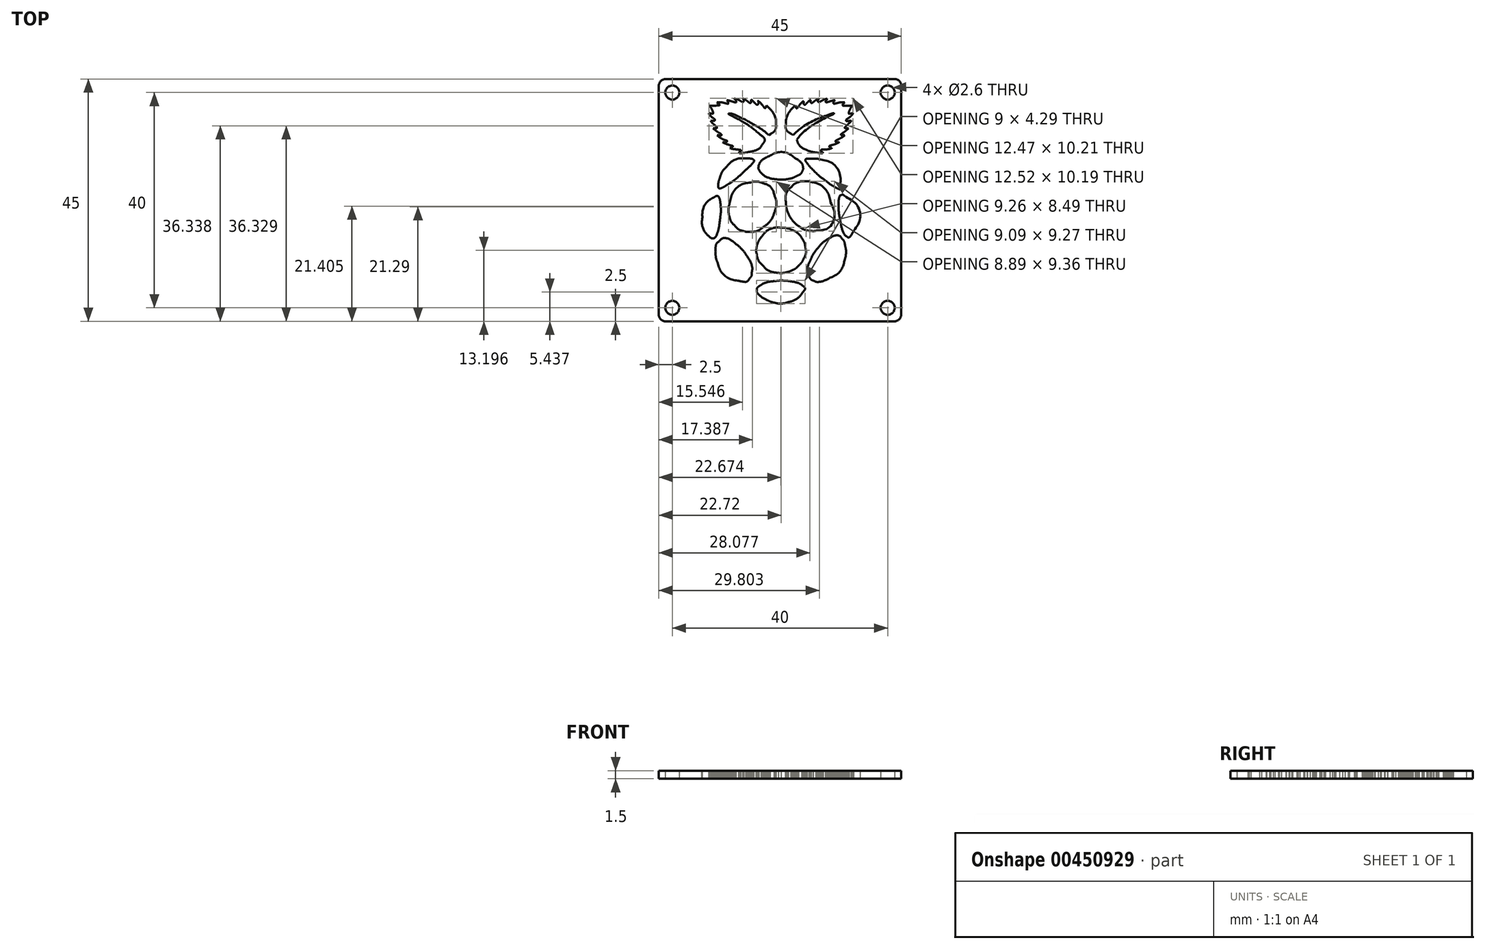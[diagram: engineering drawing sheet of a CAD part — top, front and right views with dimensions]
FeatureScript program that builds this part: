
annotation { "Feature Type Name" : "Feature", "Feature Type Description" : "" }
export const myFeature = defineFeature(function(context is Context, id is Id, definition is map)
    precondition{}
    {
        {
            var Q0;
            Q0=qCreatedBy(makeId("Top.planeOp"),FACE);
            var sketch = newSketch(context, id + "F0", { "sketchPlane" : qUnion([Q0])});
            skLineSegment(sketch, "E0.bottom", {"start": v(20, -20) * mm, "end": v(-20, -20) * mm});
            skLineSegment(sketch, "E0.top", {"start": v(20, 20) * mm, "end": v(-20, 20) * mm});
            skLineSegment(sketch, "E0.left", {"start": v(20, -20) * mm, "end": v(20, 20) * mm});
            skLineSegment(sketch, "E0.right", {"start": v(-20, -20) * mm, "end": v(-20, 20) * mm});
            skPoint(sketch, "E0.middle", {"position": v(0, 0) * mm});
            skSolve(sketch);
        }
        {
            var Q0;
            Q0=qCreatedBy(makeId("Top.planeOp"),FACE);
            var sketch = newSketch(context, id + "F1", { "sketchPlane" : qUnion([Q0])});
            skLineSegment(sketch, "E1.bottom", {"start": v(22.5, -22.5) * mm, "end": v(-22.5, -22.5) * mm});
            skLineSegment(sketch, "E1.top", {"start": v(22.5, 22.5) * mm, "end": v(-22.5, 22.5) * mm});
            skLineSegment(sketch, "E1.left", {"start": v(22.5, -22.5) * mm, "end": v(22.5, 22.5) * mm});
            skLineSegment(sketch, "E1.right", {"start": v(-22.5, -22.5) * mm, "end": v(-22.5, 22.5) * mm});
            skPoint(sketch, "E1.middle", {"position": v(0, 0) * mm});
            skSolve(sketch);
        }
        {
            var Q0;
            Q0=qCreatedBy(makeId("Top.planeOp"),FACE);
            var sketch = newSketch(context, id + "F2", { "sketchPlane" : qUnion([Q0])});
            skCircle(sketch, "E2", {"center": v(-20, 20) * mm, "radius": 1.3 * mm});
            skCircle(sketch, "E3", {"center": v(20, 20) * mm, "radius": 1.3 * mm});
            skCircle(sketch, "E4", {"center": v(-20, -20) * mm, "radius": 1.3 * mm});
            skCircle(sketch, "E5", {"center": v(20, -20) * mm, "radius": 1.3 * mm});
            skSolve(sketch);
        }
        {
            var Q0;
            Q0 = qSketchRegion(id + "F1", true);
            extrude(context, id + "F3", {"entities" : qUnion([Q0]), "depth" : 1.5 * mm, "offsetDistance" : 25 * mm});
        }
        {
            var Q0;
            Q0 = qSketchRegion(id + "F0", true);
            extrude(context, id + "F4", {"entities" : qUnion([Q0]), "operationType" : NewBodyOperationType.ADD, "depth" : 1.5 * mm, "offsetDistance" : 25 * mm});
        }
        {
            var Q0;
            Q0 = qSketchRegion(id + "F2", true);
            extrude(context, id + "F5", {"entities" : qUnion([Q0]), "operationType" : NewBodyOperationType.REMOVE, "flatOperationType" : FlatOperationType.REMOVE, "depth" : 1.5 * mm, "offsetDistance" : 25 * mm, "domain" : OperationDomain.MODEL});
        }
        {
            var Q0;
            Q0=makeQuery(id+"F3.opExtrude","SWEPT_EDGE",EDGE,{"disambiguationData":[OSD([sQuery(id+"F1.wireOp",EDGE,"E1.top"),sQuery(id+"F1.wireOp",EDGE,"E1.left")])]});
            var Q1;
            Q1=makeQuery(id+"F3.opExtrude","SWEPT_EDGE",EDGE,{"disambiguationData":[OSD([sQuery(id+"F1.wireOp",EDGE,"E1.top"),sQuery(id+"F1.wireOp",EDGE,"E1.right")])]});
            var Q2;
            Q2=makeQuery(id+"F3.opExtrude","SWEPT_EDGE",EDGE,{"disambiguationData":[OSD([sQuery(id+"F1.wireOp",EDGE,"E1.bottom"),sQuery(id+"F1.wireOp",EDGE,"E1.right")])]});
            var Q3;
            Q3=makeQuery(id+"F3.opExtrude","SWEPT_EDGE",EDGE,{"disambiguationData":[OSD([sQuery(id+"F1.wireOp",EDGE,"E1.bottom"),sQuery(id+"F1.wireOp",EDGE,"E1.left")])]});
            fillet(context, id + "F6", {"entities" : qUnion([Q0, Q1, Q2, Q3]), "radius" : 1.2 * mm, "tangentPropagation" : true, "allowEdgeOverflow" : false});
        }
        {
            var Q0;
            Q0=qCreatedBy(makeId("Top.planeOp"),FACE);
            cPlane(context, id + "F7", {"entities" : qUnion([Q0]), "cplaneType" : CPlaneType.OFFSET, "offset" : 25 * mm, "width" : 150 * mm, "height" : 150 * mm});
        }
        {
            var Q0;
            Q0=qCreatedBy(id+"F7.planeOp",FACE);
            var sketch = newSketch(context, id + "F8", { "sketchPlane" : qUnion([Q0])});
            skFitSpline(sketch, "E6", {"points": [v(-0.89, -19.07) * mm, v(-1.37, -18.96) * mm, v(-1.92, -18.78) * mm, v(-2.27, -18.6) * mm]});
            skFitSpline(sketch, "E7", {"points": [v(-2.27, -18.6) * mm, v(-3.23, -18.12) * mm, v(-4.29, -17.1) * mm, v(-4.29, -16.67) * mm]});
            skFitSpline(sketch, "E8", {"points": [v(-4.29, -16.67) * mm, v(-4.29, -16.4) * mm, v(-4, -16.06) * mm, v(-3.5, -15.74) * mm]});
            skFitSpline(sketch, "E9", {"points": [v(-3.5, -15.74) * mm, v(-2.99, -15.43) * mm, v(-1.93, -15.14) * mm, v(-0.78, -15) * mm]});
            skFitSpline(sketch, "E10", {"points": [v(-0.78, -15) * mm, v(-0.11, -14.93) * mm, v(1.32, -14.97) * mm, v(2.07, -15.1) * mm]});
            skFitSpline(sketch, "E11", {"points": [v(2.07, -15.1) * mm, v(2.83, -15.22) * mm, v(3.85, -15.59) * mm, v(4.15, -15.85) * mm]});
            skFitSpline(sketch, "E12", {"points": [v(4.15, -15.85) * mm, v(4.62, -16.25) * mm, v(4.65, -16.56) * mm, v(4.27, -17.04) * mm]});
            skFitSpline(sketch, "E13", {"points": [v(4.27, -17.04) * mm, v(3.53, -17.98) * mm, v(2.59, -18.62) * mm, v(1.46, -18.95) * mm]});
            skFitSpline(sketch, "E14", {"points": [v(1.46, -18.95) * mm, v(0.83, -19.14) * mm, v(-0.3, -19.2) * mm, v(-0.89, -19.07) * mm]});
            skFitSpline(sketch, "E15", {"points": [v(-7.64, -14.96) * mm, v(-9.38, -14.6) * mm, v(-10.94, -13.25) * mm, v(-11.6, -11.56) * mm]});
            skFitSpline(sketch, "E16", {"points": [v(-11.6, -11.56) * mm, v(-11.84, -10.92) * mm, v(-11.94, -10.32) * mm, v(-11.94, -9.57) * mm]});
            skFitSpline(sketch, "E17", {"points": [v(-11.94, -9.57) * mm, v(-11.94, -8.58) * mm, v(-11.75, -8) * mm, v(-11.3, -7.65) * mm]});
            skFitSpline(sketch, "E18", {"points": [v(-11.3, -7.65) * mm, v(-10.56, -7.05) * mm, v(-9.4, -7.25) * mm, v(-8.08, -8.22) * mm]});
            skFitSpline(sketch, "E19", {"points": [v(-8.08, -8.22) * mm, v(-7.62, -8.56) * mm, v(-6.63, -9.62) * mm, v(-6.3, -10.13) * mm]});
            skFitSpline(sketch, "E20", {"points": [v(-6.3, -10.13) * mm, v(-5.55, -11.3) * mm, v(-5.15, -12.47) * mm, v(-5.22, -13.34) * mm]});
            skFitSpline(sketch, "E21", {"points": [v(-5.22, -13.34) * mm, v(-5.26, -13.97) * mm, v(-5.32, -14.14) * mm, v(-5.61, -14.51) * mm]});
            skFitSpline(sketch, "E22", {"points": [v(-5.61, -14.51) * mm, v(-6.04, -15.06) * mm, v(-6.6, -15.18) * mm, v(-7.64, -14.96) * mm]});
            skFitSpline(sketch, "E23", {"points": [v(6.26, -14.97) * mm, v(5.9, -14.83) * mm, v(5.61, -14.57) * mm, v(5.42, -14.18) * mm]});
            skFitSpline(sketch, "E24", {"points": [v(5.42, -14.18) * mm, v(5.14, -13.6) * mm, v(5.2, -12.22) * mm, v(5.54, -11.43) * mm]});
            skFitSpline(sketch, "E25", {"points": [v(5.54, -11.43) * mm, v(5.58, -11.33) * mm, v(5.68, -11.09) * mm, v(5.76, -10.9) * mm]});
            skFitSpline(sketch, "E26", {"points": [v(5.76, -10.9) * mm, v(5.95, -10.44) * mm, v(6.61, -9.4) * mm, v(7.07, -8.84) * mm]});
            skFitSpline(sketch, "E27", {"points": [v(7.07, -8.84) * mm, v(7.54, -8.27) * mm, v(8.45, -7.48) * mm, v(9, -7.17) * mm]});
            skFitSpline(sketch, "E28", {"points": [v(9, -7.17) * mm, v(10.02, -6.6) * mm, v(11, -6.6) * mm, v(11.53, -7.15) * mm]});
            skFitSpline(sketch, "E29", {"points": [v(11.53, -7.15) * mm, v(11.81, -7.46) * mm, v(12, -7.92) * mm, v(12.15, -8.71) * mm]});
            skFitSpline(sketch, "E30", {"points": [v(12.15, -8.71) * mm, v(12.26, -9.3) * mm, v(12.19, -10.46) * mm, v(12, -11.07) * mm]});
            skFitSpline(sketch, "E31", {"points": [v(12, -11.07) * mm, v(11.55, -12.6) * mm, v(10.56, -13.78) * mm, v(9.13, -14.49) * mm]});
            skFitSpline(sketch, "E32", {"points": [v(9.13, -14.49) * mm, v(8.17, -14.97) * mm, v(6.87, -15.18) * mm, v(6.26, -14.97) * mm]});
            skFitSpline(sketch, "E33", {"points": [v(-0.24, -13.5) * mm, v(-1.52, -13.32) * mm, v(-2.45, -12.9) * mm, v(-3.16, -12.15) * mm]});
            skFitSpline(sketch, "E34", {"points": [v(-3.16, -12.15) * mm, v(-3.83, -11.45) * mm, v(-4.16, -10.82) * mm, v(-4.34, -9.89) * mm]});
            skFitSpline(sketch, "E35", {"points": [v(-4.34, -9.89) * mm, v(-4.4, -9.51) * mm, v(-4.32, -8.56) * mm, v(-4.17, -8.13) * mm]});
            skFitSpline(sketch, "E36", {"points": [v(-4.17, -8.13) * mm, v(-4.04, -7.74) * mm, v(-3.6, -6.98) * mm, v(-3.3, -6.65) * mm]});
            skFitSpline(sketch, "E37", {"points": [v(-3.3, -6.65) * mm, v(-2.5, -5.73) * mm, v(-1.04, -5.1) * mm, v(0.26, -5.1) * mm]});
            skFitSpline(sketch, "E38", {"points": [v(0.26, -5.1) * mm, v(0.76, -5.1) * mm, v(1.69, -5.3) * mm, v(2.2, -5.51) * mm]});
            skFitSpline(sketch, "E39", {"points": [v(2.2, -5.51) * mm, v(2.86, -5.79) * mm, v(3.66, -6.46) * mm, v(4.07, -7.1) * mm]});
            skFitSpline(sketch, "E40", {"points": [v(4.07, -7.1) * mm, v(4.44, -7.66) * mm, v(4.6, -8.02) * mm, v(4.7, -8.63) * mm]});
            skFitSpline(sketch, "E41", {"points": [v(4.7, -8.63) * mm, v(4.85, -9.48) * mm, v(4.74, -10.17) * mm, v(4.31, -11.04) * mm]});
            skFitSpline(sketch, "E42", {"points": [v(4.31, -11.04) * mm, v(4.11, -11.45) * mm, v(3.98, -11.62) * mm, v(3.5, -12.1) * mm]});
            skFitSpline(sketch, "E43", {"points": [v(3.5, -12.1) * mm, v(3, -12.6) * mm, v(2.87, -12.7) * mm, v(2.34, -12.96) * mm]});
            skFitSpline(sketch, "E44", {"points": [v(2.34, -12.96) * mm, v(2.02, -13.13) * mm, v(1.54, -13.3) * mm, v(1.3, -13.37) * mm]});
            skFitSpline(sketch, "E45", {"points": [v(1.3, -13.37) * mm, v(0.83, -13.48) * mm, v(0.06, -13.55) * mm, v(-0.24, -13.5) * mm]});
            skFitSpline(sketch, "E46", {"points": [v(-13.18, -6.7) * mm, v(-14, -5.84) * mm, v(-14.48, -4.45) * mm, v(-14.4, -3.23) * mm]});
            skFitSpline(sketch, "E47", {"points": [v(-14.4, -3.23) * mm, v(-14.32, -1.7) * mm, v(-13.48, -0.26) * mm, v(-12.2, 0.58) * mm]});
            skFitSpline(sketch, "E48", {"points": [v(-12.2, 0.58) * mm, v(-12.01, 0.7) * mm, v(-11.82, 0.8) * mm, v(-11.77, 0.8) * mm]});
            skFitSpline(sketch, "E49", {"points": [v(-11.77, 0.8) * mm, v(-11.5, 0.8) * mm, v(-11.2, 0.21) * mm, v(-11.09, -0.45) * mm]});
            skFitSpline(sketch, "E50", {"points": [v(-11.09, -0.45) * mm, v(-11.02, -0.92) * mm, v(-11, -2.43) * mm, v(-11.06, -2.86) * mm]});
            skFitSpline(sketch, "E51", {"points": [v(-11.06, -2.86) * mm, v(-11.38, -5.19) * mm, v(-12.15, -7.03) * mm, v(-12.8, -7.03) * mm]});
            skFitSpline(sketch, "E52", {"points": [v(-12.8, -7.03) * mm, v(-12.83, -7.03) * mm, v(-13, -6.88) * mm, v(-13.18, -6.7) * mm]});
            skFitSpline(sketch, "E53", {"points": [v(12.4, -6.74) * mm, v(11.97, -6.36) * mm, v(11.48, -5.18) * mm, v(11.23, -3.94) * mm]});
            skFitSpline(sketch, "E54", {"points": [v(11.23, -3.94) * mm, v(11.04, -3) * mm, v(10.9, -1.78) * mm, v(10.9, -1.14) * mm]});
            skFitSpline(sketch, "E55", {"points": [v(10.9, -1.14) * mm, v(10.9, -0.09) * mm, v(11.13, 0.83) * mm, v(11.42, 0.97) * mm]});
            skFitSpline(sketch, "E56", {"points": [v(11.42, 0.97) * mm, v(11.59, 1.04) * mm, v(11.84, 0.93) * mm, v(12.3, 0.6) * mm]});
            skFitSpline(sketch, "E57", {"points": [v(12.3, 0.6) * mm, v(14.3, -0.91) * mm, v(14.88, -3.45) * mm, v(13.72, -5.6) * mm]});
            skFitSpline(sketch, "E58", {"points": [v(13.72, -5.6) * mm, v(13.4, -6.22) * mm, v(12.82, -6.91) * mm, v(12.64, -6.91) * mm]});
            skFitSpline(sketch, "E59", {"points": [v(12.64, -6.91) * mm, v(12.62, -6.91) * mm, v(12.51, -6.83) * mm, v(12.4, -6.74) * mm]});
            skFitSpline(sketch, "E60", {"points": [v(-6.67, -5.76) * mm, v(-7.4, -5.56) * mm, v(-7.81, -5.32) * mm, v(-8.37, -4.76) * mm]});
            skFitSpline(sketch, "E61", {"points": [v(-8.37, -4.76) * mm, v(-8.9, -4.23) * mm, v(-9.18, -3.75) * mm, v(-9.37, -3.06) * mm]});
            skFitSpline(sketch, "E62", {"points": [v(-9.37, -3.06) * mm, v(-9.52, -2.5) * mm, v(-9.5, -1.2) * mm, v(-9.34, -0.62) * mm]});
            skFitSpline(sketch, "E63", {"points": [v(-9.34, -0.62) * mm, v(-8.79, 1.32) * mm, v(-7.3, 2.83) * mm, v(-5.48, 3.3) * mm]});
            skFitSpline(sketch, "E64", {"points": [v(-5.48, 3.3) * mm, v(-4.87, 3.45) * mm, v(-3.93, 3.42) * mm, v(-3.42, 3.24) * mm]});
            skFitSpline(sketch, "E65", {"points": [v(-3.42, 3.24) * mm, v(-2.14, 2.78) * mm, v(-1.41, 2.02) * mm, v(-0.97, 0.7) * mm]});
            skFitSpline(sketch, "E66", {"points": [v(-0.97, 0.7) * mm, v(-0.7, -0.09) * mm, v(-0.74, -1.3) * mm, v(-1.05, -2.21) * mm]});
            skFitSpline(sketch, "E67", {"points": [v(-1.05, -2.21) * mm, v(-1.4, -3.23) * mm, v(-2.17, -4.28) * mm, v(-3.04, -4.93) * mm]});
            skFitSpline(sketch, "E68", {"points": [v(-3.04, -4.93) * mm, v(-3.86, -5.54) * mm, v(-4.65, -5.83) * mm, v(-5.59, -5.87) * mm]});
            skFitSpline(sketch, "E69", {"points": [v(-5.59, -5.87) * mm, v(-6.09, -5.9) * mm, v(-6.26, -5.87) * mm, v(-6.67, -5.76) * mm]});
            skFitSpline(sketch, "E70", {"points": [v(5.69, -5.68) * mm, v(5, -5.61) * mm, v(4.16, -5.28) * mm, v(3.48, -4.81) * mm]});
            skFitSpline(sketch, "E71", {"points": [v(3.48, -4.81) * mm, v(3.16, -4.6) * mm, v(2.43, -3.88) * mm, v(2.16, -3.51) * mm]});
            skFitSpline(sketch, "E72", {"points": [v(2.16, -3.51) * mm, v(1.91, -3.18) * mm, v(1.37, -2.04) * mm, v(1.26, -1.61) * mm]});
            skFitSpline(sketch, "E73", {"points": [v(1.26, -1.61) * mm, v(1.2, -1.4) * mm, v(1.13, -0.92) * mm, v(1.12, -0.57) * mm]});
            skFitSpline(sketch, "E74", {"points": [v(1.12, -0.57) * mm, v(1.05, 0.72) * mm, v(1.4, 1.72) * mm, v(2.22, 2.57) * mm]});
            skFitSpline(sketch, "E75", {"points": [v(2.22, 2.57) * mm, v(2.58, 2.93) * mm, v(2.92, 3.15) * mm, v(3.5, 3.38) * mm]});
            skFitSpline(sketch, "E76", {"points": [v(3.5, 3.38) * mm, v(3.86, 3.52) * mm, v(3.98, 3.54) * mm, v(4.6, 3.54) * mm]});
            skFitSpline(sketch, "E77", {"points": [v(4.6, 3.54) * mm, v(5.2, 3.54) * mm, v(5.39, 3.52) * mm, v(5.74, 3.4) * mm]});
            skFitSpline(sketch, "E78", {"points": [v(5.74, 3.4) * mm, v(7.47, 2.87) * mm, v(8.85, 1.45) * mm, v(9.39, -0.34) * mm]});
            skFitSpline(sketch, "E79", {"points": [v(9.39, -0.34) * mm, v(10.14, -2.83) * mm, v(9, -5.13) * mm, v(6.78, -5.63) * mm]});
            skFitSpline(sketch, "E80", {"points": [v(6.78, -5.63) * mm, v(6.4, -5.72) * mm, v(6.14, -5.73) * mm, v(5.69, -5.68) * mm]});
            skFitSpline(sketch, "E81", {"points": [v(10.42, 2.35) * mm, v(9.77, 2.7) * mm, v(9.34, 2.96) * mm, v(8.91, 3.29) * mm]});
            skFitSpline(sketch, "E82", {"points": [v(8.91, 3.29) * mm, v(8.71, 3.44) * mm, v(8.32, 3.75) * mm, v(8.04, 3.96) * mm]});
            skFitSpline(sketch, "E83", {"points": [v(8.04, 3.96) * mm, v(7.28, 4.53) * mm, v(5.7, 6.07) * mm, v(5.11, 6.8) * mm]});
            skFitSpline(sketch, "E84", {"points": [v(5.11, 6.8) * mm, v(4.86, 7.11) * mm, v(4.7, 7.4) * mm, v(4.74, 7.5) * mm]});
            skFitSpline(sketch, "E85", {"points": [v(4.74, 7.5) * mm, v(4.8, 7.65) * mm, v(5.35, 7.73) * mm, v(6.17, 7.73) * mm]});
            skFitSpline(sketch, "E86", {"points": [v(6.17, 7.73) * mm, v(6.85, 7.72) * mm, v(7.03, 7.7) * mm, v(7.46, 7.57) * mm]});
            skFitSpline(sketch, "E87", {"points": [v(7.46, 7.57) * mm, v(9.63, 6.92) * mm, v(11.05, 5.14) * mm, v(11.22, 2.88) * mm]});
            skFitSpline(sketch, "E88", {"points": [v(11.22, 2.88) * mm, v(11.24, 2.61) * mm, v(11.24, 2.33) * mm, v(11.22, 2.25) * mm]});
            skFitSpline(sketch, "E89", {"points": [v(11.22, 2.25) * mm, v(11.16, 2.03) * mm, v(10.96, 2.06) * mm, v(10.42, 2.35) * mm]});
            skFitSpline(sketch, "E90", {"points": [v(-11.4, 2.3) * mm, v(-11.5, 2.57) * mm, v(-11.35, 3.6) * mm, v(-11.12, 4.28) * mm]});
            skFitSpline(sketch, "E91", {"points": [v(-11.12, 4.28) * mm, v(-10.85, 5.07) * mm, v(-10.48, 5.66) * mm, v(-9.84, 6.3) * mm]});
            skFitSpline(sketch, "E92", {"points": [v(-9.84, 6.3) * mm, v(-8.89, 7.24) * mm, v(-7.6, 7.77) * mm, v(-6.25, 7.76) * mm]});
            skFitSpline(sketch, "E93", {"points": [v(-6.25, 7.76) * mm, v(-5.72, 7.76) * mm, v(-5.06, 7.65) * mm, v(-4.96, 7.55) * mm]});
            skFitSpline(sketch, "E94", {"points": [v(-4.96, 7.55) * mm, v(-4.78, 7.37) * mm, v(-5.52, 6.4) * mm, v(-6.64, 5.36) * mm]});
            skFitSpline(sketch, "E95", {"points": [v(-6.64, 5.36) * mm, v(-7.54, 4.53) * mm, v(-8.96, 3.38) * mm, v(-9.5, 3.06) * mm]});
            skFitSpline(sketch, "E96", {"points": [v(-9.5, 3.06) * mm, v(-9.67, 2.95) * mm, v(-9.95, 2.78) * mm, v(-10.11, 2.67) * mm]});
            skFitSpline(sketch, "E97", {"points": [v(-10.11, 2.67) * mm, v(-10.46, 2.46) * mm, v(-11.05, 2.21) * mm, v(-11.23, 2.21) * mm]});
            skFitSpline(sketch, "E98", {"points": [v(-11.23, 2.21) * mm, v(-11.3, 2.21) * mm, v(-11.37, 2.25) * mm, v(-11.4, 2.3) * mm]});
            skFitSpline(sketch, "E99", {"points": [v(-0.76, 3.91) * mm, v(-1.66, 4.03) * mm, v(-2.9, 4.54) * mm, v(-3.41, 5) * mm]});
            skFitSpline(sketch, "E100", {"points": [v(-3.41, 5) * mm, v(-3.57, 5.14) * mm, v(-3.76, 5.4) * mm, v(-3.85, 5.58) * mm]});
            skFitSpline(sketch, "E101", {"points": [v(-3.85, 5.58) * mm, v(-4, 5.86) * mm, v(-4.01, 5.95) * mm, v(-3.99, 6.2) * mm]});
            skFitSpline(sketch, "E102", {"points": [v(-3.99, 6.2) * mm, v(-3.97, 6.37) * mm, v(-3.91, 6.59) * mm, v(-3.86, 6.7) * mm]});
            skFitSpline(sketch, "E103", {"points": [v(-3.86, 6.7) * mm, v(-3.62, 7.15) * mm, v(-2.73, 7.86) * mm, v(-1.94, 8.21) * mm]});
            skFitSpline(sketch, "E104", {"points": [v(-1.94, 8.21) * mm, v(-0.43, 8.9) * mm, v(1.35, 8.75) * mm, v(2.77, 7.85) * mm]});
            skFitSpline(sketch, "E105", {"points": [v(2.77, 7.85) * mm, v(3.6, 7.32) * mm, v(4.16, 6.68) * mm, v(4.27, 6.15) * mm]});
            skFitSpline(sketch, "E106", {"points": [v(4.27, 6.15) * mm, v(4.33, 5.88) * mm, v(4.32, 5.81) * mm, v(4.22, 5.58) * mm]});
            skFitSpline(sketch, "E107", {"points": [v(4.22, 5.58) * mm, v(3.98, 5.04) * mm, v(3.7, 4.78) * mm, v(2.94, 4.42) * mm]});
            skFitSpline(sketch, "E108", {"points": [v(2.94, 4.42) * mm, v(2.37, 4.15) * mm, v(2.15, 4.07) * mm, v(1.6, 3.97) * mm]});
            skFitSpline(sketch, "E109", {"points": [v(1.6, 3.97) * mm, v(0.92, 3.85) * mm, v(-0.06, 3.82) * mm, v(-0.76, 3.91) * mm]});
            skFitSpline(sketch, "E110", {"points": [v(-7.58, 8.81) * mm, v(-7.6, 8.83) * mm, v(-7.55, 8.91) * mm, v(-7.46, 9) * mm]});
            skFitSpline(sketch, "E111", {"points": [v(-7.46, 9) * mm, v(-7.36, 9.07) * mm, v(-7.29, 9.18) * mm, v(-7.29, 9.24) * mm]});
            skFitSpline(sketch, "E112", {"points": [v(-7.29, 9.24) * mm, v(-7.29, 9.36) * mm, v(-7.31, 9.36) * mm, v(-8.22, 9.46) * mm]});
            skFitSpline(sketch, "E113", {"points": [v(-8.22, 9.46) * mm, v(-8.54, 9.49) * mm, v(-8.9, 9.55) * mm, v(-9.05, 9.6) * mm]});
            skFitSpline(sketch, "E114", {"points": [v(-9.07, 9.78) * mm, v(-8.8, 9.9) * mm, v(-8.77, 10.08) * mm, v(-8.99, 10.15) * mm]});
            skFitSpline(sketch, "E115", {"points": [v(-8.99, 10.15) * mm, v(-9.54, 10.3) * mm, v(-10.3, 10.57) * mm, v(-10.46, 10.66) * mm]});
            skLineSegment(sketch, "E116", {"start": v(-9.05, 9.6) * mm, "end": v(-9.3, 9.67) * mm});
            skLineSegment(sketch, "E117", {"start": v(-9.3, 9.67) * mm, "end": v(-9.07, 9.78) * mm});
            skLineSegment(sketch, "E118", {"start": v(-9.07, 9.78) * mm, "end": v(-9.05, 9.6) * mm});
            skFitSpline(sketch, "E119", {"points": [v(-10.48, 10.76) * mm, v(-10, 10.77) * mm, v(-9.84, 11.02) * mm, v(-10.24, 11.18) * mm]});
            skFitSpline(sketch, "E120", {"points": [v(-10.24, 11.18) * mm, v(-10.53, 11.3) * mm, v(-11.28, 11.73) * mm, v(-11.51, 11.92) * mm]});
            skLineSegment(sketch, "E121", {"start": v(-10.46, 10.66) * mm, "end": v(-10.66, 10.76) * mm});
            skLineSegment(sketch, "E122", {"start": v(-10.66, 10.76) * mm, "end": v(-10.48, 10.76) * mm});
            skLineSegment(sketch, "E123", {"start": v(-10.48, 10.76) * mm, "end": v(-10.46, 10.66) * mm});
            skFitSpline(sketch, "E124", {"points": [v(-11.44, 12.07) * mm, v(-10.89, 12.07) * mm, v(-10.9, 12.23) * mm, v(-11.47, 12.62) * mm]});
            skFitSpline(sketch, "E125", {"points": [v(-11.47, 12.62) * mm, v(-11.71, 12.78) * mm, v(-12.02, 13.02) * mm, v(-12.16, 13.14) * mm]});
            skLineSegment(sketch, "E126", {"start": v(-11.51, 11.92) * mm, "end": v(-11.68, 12.06) * mm});
            skLineSegment(sketch, "E127", {"start": v(-11.68, 12.06) * mm, "end": v(-11.44, 12.07) * mm});
            skLineSegment(sketch, "E128", {"start": v(-11.44, 12.07) * mm, "end": v(-11.51, 11.92) * mm});
            skFitSpline(sketch, "E129", {"points": [v(-12.15, 13.37) * mm, v(-11.85, 13.37) * mm, v(-11.7, 13.41) * mm, v(-11.7, 13.5) * mm]});
            skFitSpline(sketch, "E130", {"points": [v(-11.7, 13.5) * mm, v(-11.7, 13.54) * mm, v(-11.92, 13.77) * mm, v(-12.19, 14.01) * mm]});
            skFitSpline(sketch, "E131", {"points": [v(-12.19, 14.01) * mm, v(-12.45, 14.25) * mm, v(-12.72, 14.52) * mm, v(-12.78, 14.6) * mm]});
            skLineSegment(sketch, "E132", {"start": v(-12.16, 13.14) * mm, "end": v(-12.42, 13.37) * mm});
            skLineSegment(sketch, "E133", {"start": v(-12.42, 13.37) * mm, "end": v(-12.15, 13.37) * mm});
            skLineSegment(sketch, "E134", {"start": v(-12.15, 13.37) * mm, "end": v(-12.16, 13.14) * mm});
            skFitSpline(sketch, "E135", {"points": [v(-12.51, 14.76) * mm, v(-12.15, 14.76) * mm, v(-12.13, 14.77) * mm, v(-12.12, 14.9) * mm]});
            skFitSpline(sketch, "E136", {"points": [v(-12.12, 14.9) * mm, v(-12.1, 15.01) * mm, v(-12.16, 15.08) * mm, v(-12.34, 15.21) * mm]});
            skFitSpline(sketch, "E137", {"points": [v(-12.34, 15.21) * mm, v(-12.62, 15.42) * mm, v(-13.18, 16) * mm, v(-13.18, 16.1) * mm]});
            skFitSpline(sketch, "E138", {"points": [v(-13.18, 16.1) * mm, v(-13.18, 16.14) * mm, v(-13.08, 16.15) * mm, v(-12.81, 16.12) * mm]});
            skFitSpline(sketch, "E139", {"points": [v(-12.81, 16.12) * mm, v(-12.45, 16.08) * mm, v(-12.45, 16.08) * mm, v(-12.45, 16.21) * mm]});
            skFitSpline(sketch, "E140", {"points": [v(-12.45, 16.21) * mm, v(-12.45, 16.39) * mm, v(-12.8, 17.18) * mm, v(-12.97, 17.41) * mm]});
            skLineSegment(sketch, "E141", {"start": v(-12.78, 14.6) * mm, "end": v(-12.89, 14.76) * mm});
            skLineSegment(sketch, "E142", {"start": v(-12.89, 14.76) * mm, "end": v(-12.51, 14.76) * mm});
            skLineSegment(sketch, "E143", {"start": v(-12.51, 14.76) * mm, "end": v(-12.78, 14.6) * mm});
            skFitSpline(sketch, "E144", {"points": [v(-12.62, 17.57) * mm, v(-12.35, 17.56) * mm, v(-11.95, 17.57) * mm, v(-11.72, 17.6) * mm]});
            skFitSpline(sketch, "E145", {"points": [v(-11.72, 17.6) * mm, v(-11.24, 17.64) * mm, v(-11.2, 17.7) * mm, v(-11.51, 18) * mm]});
            skLineSegment(sketch, "E146", {"start": v(-12.97, 17.41) * mm, "end": v(-13.11, 17.6) * mm});
            skLineSegment(sketch, "E147", {"start": v(-13.11, 17.6) * mm, "end": v(-12.62, 17.57) * mm});
            skLineSegment(sketch, "E148", {"start": v(-12.62, 17.57) * mm, "end": v(-12.97, 17.41) * mm});
            skFitSpline(sketch, "E149", {"points": [v(-11.24, 18.19) * mm, v(-10.95, 18.19) * mm, v(-10.6, 18.14) * mm, v(-10.32, 18.07) * mm]});
            skFitSpline(sketch, "E150", {"points": [v(-10.32, 18.07) * mm, v(-9.69, 17.91) * mm, v(-9.61, 17.92) * mm, v(-9.61, 18.14) * mm]});
            skFitSpline(sketch, "E151", {"points": [v(-9.61, 18.14) * mm, v(-9.61, 18.25) * mm, v(-9.66, 18.38) * mm, v(-9.74, 18.46) * mm]});
            skLineSegment(sketch, "E152", {"start": v(-11.51, 18) * mm, "end": v(-11.72, 18.19) * mm});
            skLineSegment(sketch, "E153", {"start": v(-11.72, 18.19) * mm, "end": v(-11.24, 18.19) * mm});
            skLineSegment(sketch, "E154", {"start": v(-11.24, 18.19) * mm, "end": v(-11.51, 18) * mm});
            skFitSpline(sketch, "E155", {"points": [v(-9.64, 18.55) * mm, v(-9.52, 18.53) * mm, v(-9.18, 18.44) * mm, v(-8.9, 18.35) * mm]});
            skFitSpline(sketch, "E156", {"points": [v(-8.9, 18.35) * mm, v(-8.61, 18.26) * mm, v(-8.34, 18.19) * mm, v(-8.29, 18.19) * mm]});
            skFitSpline(sketch, "E157", {"points": [v(-8.29, 18.19) * mm, v(-8.14, 18.19) * mm, v(-8.17, 18.5) * mm, v(-8.34, 18.7) * mm]});
            skFitSpline(sketch, "E158", {"points": [v(-8.34, 18.7) * mm, v(-8.42, 18.79) * mm, v(-8.46, 18.87) * mm, v(-8.43, 18.87) * mm]});
            skFitSpline(sketch, "E159", {"points": [v(-8.43, 18.87) * mm, v(-8.3, 18.87) * mm, v(-7.47, 18.54) * mm, v(-7.24, 18.4) * mm]});
            skFitSpline(sketch, "E160", {"points": [v(-7.24, 18.4) * mm, v(-7.1, 18.3) * mm, v(-6.96, 18.25) * mm, v(-6.9, 18.26) * mm]});
            skFitSpline(sketch, "E161", {"points": [v(-6.9, 18.26) * mm, v(-6.79, 18.28) * mm, v(-6.74, 18.64) * mm, v(-6.84, 18.82) * mm]});
            skFitSpline(sketch, "E162", {"points": [v(-6.84, 18.82) * mm, v(-6.9, 18.93) * mm, v(-6.89, 18.93) * mm, v(-6.62, 18.78) * mm]});
            skFitSpline(sketch, "E163", {"points": [v(-6.62, 18.78) * mm, v(-6.46, 18.7) * mm, v(-6.17, 18.5) * mm, v(-5.99, 18.35) * mm]});
            skFitSpline(sketch, "E164", {"points": [v(-5.99, 18.35) * mm, v(-5.8, 18.2) * mm, v(-5.61, 18.07) * mm, v(-5.57, 18.07) * mm]});
            skFitSpline(sketch, "E165", {"points": [v(-5.57, 18.07) * mm, v(-5.44, 18.07) * mm, v(-5.36, 18.2) * mm, v(-5.36, 18.43) * mm]});
            skFitSpline(sketch, "E166", {"points": [v(-5.36, 18.43) * mm, v(-5.36, 18.55) * mm, v(-5.34, 18.64) * mm, v(-5.3, 18.64) * mm]});
            skFitSpline(sketch, "E167", {"points": [v(-5.3, 18.64) * mm, v(-5.26, 18.64) * mm, v(-5.03, 18.44) * mm, v(-4.78, 18.19) * mm]});
            skFitSpline(sketch, "E168", {"points": [v(-4.78, 18.19) * mm, v(-4.45, 17.86) * mm, v(-4.3, 17.74) * mm, v(-4.23, 17.76) * mm]});
            skFitSpline(sketch, "E169", {"points": [v(-4.23, 17.76) * mm, v(-4.1, 17.8) * mm, v(-3.98, 18.15) * mm, v(-4.02, 18.31) * mm]});
            skFitSpline(sketch, "E170", {"points": [v(-4.02, 18.31) * mm, v(-4.06, 18.46) * mm, v(-3.37, 17.79) * mm, v(-3.05, 17.38) * mm]});
            skFitSpline(sketch, "E171", {"points": [v(-3.05, 17.38) * mm, v(-2.94, 17.23) * mm, v(-2.8, 17.11) * mm, v(-2.76, 17.12) * mm]});
            skFitSpline(sketch, "E172", {"points": [v(-2.76, 17.12) * mm, v(-2.72, 17.13) * mm, v(-2.64, 17.25) * mm, v(-2.6, 17.4) * mm]});
            skLineSegment(sketch, "E173", {"start": v(-9.74, 18.46) * mm, "end": v(-9.87, 18.6) * mm});
            skLineSegment(sketch, "E174", {"start": v(-9.87, 18.6) * mm, "end": v(-9.64, 18.55) * mm});
            skLineSegment(sketch, "E175", {"start": v(-9.64, 18.55) * mm, "end": v(-9.74, 18.46) * mm});
            skFitSpline(sketch, "E176", {"points": [v(-2.24, 17.34) * mm, v(-1.4, 16.44) * mm, v(-0.75, 14.97) * mm, v(-0.75, 14.02) * mm]});
            skFitSpline(sketch, "E177", {"points": [v(-0.75, 14.02) * mm, v(-0.76, 13.33) * mm, v(-1.1, 12.75) * mm, v(-1.78, 12.32) * mm]});
            skLineSegment(sketch, "E178", {"start": v(-2.6, 17.4) * mm, "end": v(-2.51, 17.64) * mm});
            skLineSegment(sketch, "E179", {"start": v(-2.51, 17.64) * mm, "end": v(-2.24, 17.34) * mm});
            skLineSegment(sketch, "E180", {"start": v(-2.24, 17.34) * mm, "end": v(-2.6, 17.4) * mm});
            skFitSpline(sketch, "E181", {"points": [v(-2.54, 12.5) * mm, v(-3.1, 12.96) * mm, v(-4.37, 13.8) * mm, v(-5.2, 14.25) * mm]});
            skFitSpline(sketch, "E182", {"points": [v(-5.2, 14.25) * mm, v(-6.4, 14.92) * mm, v(-9.02, 16.1) * mm, v(-9.33, 16.1) * mm]});
            skFitSpline(sketch, "E183", {"points": [v(-9.33, 16.1) * mm, v(-9.57, 16.1) * mm, v(-9.43, 15.94) * mm, v(-8.98, 15.7) * mm]});
            skFitSpline(sketch, "E184", {"points": [v(-8.98, 15.7) * mm, v(-7.16, 14.73) * mm, v(-5.37, 13.59) * mm, v(-4.17, 12.61) * mm]});
            skFitSpline(sketch, "E185", {"points": [v(-4.17, 12.61) * mm, v(-3.53, 12.1) * mm, v(-2.81, 11.39) * mm, v(-2.81, 11.27) * mm]});
            skFitSpline(sketch, "E186", {"points": [v(-2.81, 11.27) * mm, v(-2.81, 11.1) * mm, v(-2.99, 10.75) * mm, v(-3.25, 10.38) * mm]});
            skFitSpline(sketch, "E187", {"points": [v(-3.25, 10.38) * mm, v(-3.75, 9.67) * mm, v(-4.54, 9.25) * mm, v(-5.9, 8.96) * mm]});
            skFitSpline(sketch, "E188", {"points": [v(-5.9, 8.96) * mm, v(-6.47, 8.83) * mm, v(-7.52, 8.74) * mm, v(-7.58, 8.81) * mm]});
            skLineSegment(sketch, "E189", {"start": v(-1.78, 12.32) * mm, "end": v(-2.07, 12.12) * mm});
            skLineSegment(sketch, "E190", {"start": v(-2.07, 12.12) * mm, "end": v(-2.54, 12.5) * mm});
            skLineSegment(sketch, "E191", {"start": v(-2.54, 12.5) * mm, "end": v(-1.78, 12.32) * mm});
            skFitSpline(sketch, "E192", {"points": [v(6.68, 8.87) * mm, v(6, 8.98) * mm, v(5.24, 9.2) * mm, v(4.74, 9.44) * mm]});
            skFitSpline(sketch, "E193", {"points": [v(4.74, 9.44) * mm, v(4.06, 9.76) * mm, v(3.44, 10.42) * mm, v(3.22, 11.04) * mm]});
            skFitSpline(sketch, "E194", {"points": [v(3.31, 11.5) * mm, v(4.28, 12.61) * mm, v(7.32, 14.71) * mm, v(9.55, 15.81) * mm]});
            skFitSpline(sketch, "E195", {"points": [v(9.55, 15.81) * mm, v(9.92, 16) * mm, v(10.05, 16.15) * mm, v(9.84, 16.15) * mm]});
            skFitSpline(sketch, "E196", {"points": [v(9.84, 16.15) * mm, v(9.78, 16.15) * mm, v(9.5, 16.06) * mm, v(9.23, 15.95) * mm]});
            skFitSpline(sketch, "E197", {"points": [v(9.23, 15.95) * mm, v(6.77, 15.03) * mm, v(4.17, 13.59) * mm, v(2.62, 12.3) * mm]});
            skLineSegment(sketch, "E198", {"start": v(3.22, 11.04) * mm, "end": v(3.14, 11.29) * mm});
            skLineSegment(sketch, "E199", {"start": v(3.14, 11.29) * mm, "end": v(3.31, 11.5) * mm});
            skLineSegment(sketch, "E200", {"start": v(3.31, 11.5) * mm, "end": v(3.22, 11.04) * mm});
            skFitSpline(sketch, "E201", {"points": [v(2.05, 12.37) * mm, v(1.36, 12.83) * mm, v(1.06, 13.43) * mm, v(1.11, 14.21) * mm]});
            skFitSpline(sketch, "E202", {"points": [v(1.11, 14.21) * mm, v(1.18, 15.19) * mm, v(1.84, 16.56) * mm, v(2.66, 17.42) * mm]});
            skLineSegment(sketch, "E203", {"start": v(2.62, 12.3) * mm, "end": v(2.41, 12.12) * mm});
            skLineSegment(sketch, "E204", {"start": v(2.41, 12.12) * mm, "end": v(2.05, 12.37) * mm});
            skLineSegment(sketch, "E205", {"start": v(2.05, 12.37) * mm, "end": v(2.62, 12.3) * mm});
            skFitSpline(sketch, "E206", {"points": [v(2.93, 17.42) * mm, v(3.02, 17.1) * mm, v(3.17, 17.1) * mm, v(3.42, 17.4) * mm]});
            skFitSpline(sketch, "E207", {"points": [v(3.42, 17.4) * mm, v(3.69, 17.75) * mm, v(4.28, 18.36) * mm, v(4.33, 18.36) * mm]});
            skFitSpline(sketch, "E208", {"points": [v(4.33, 18.36) * mm, v(4.36, 18.36) * mm, v(4.38, 18.26) * mm, v(4.38, 18.14) * mm]});
            skFitSpline(sketch, "E209", {"points": [v(4.38, 18.14) * mm, v(4.38, 17.94) * mm, v(4.5, 17.73) * mm, v(4.63, 17.73) * mm]});
            skFitSpline(sketch, "E210", {"points": [v(4.63, 17.73) * mm, v(4.65, 17.73) * mm, v(4.88, 17.94) * mm, v(5.12, 18.19) * mm]});
            skFitSpline(sketch, "E211", {"points": [v(5.12, 18.19) * mm, v(5.37, 18.44) * mm, v(5.6, 18.64) * mm, v(5.63, 18.64) * mm]});
            skFitSpline(sketch, "E212", {"points": [v(5.63, 18.64) * mm, v(5.66, 18.64) * mm, v(5.69, 18.58) * mm, v(5.69, 18.5) * mm]});
            skFitSpline(sketch, "E213", {"points": [v(5.69, 18.5) * mm, v(5.69, 18.3) * mm, v(5.79, 18.07) * mm, v(5.88, 18.07) * mm]});
            skFitSpline(sketch, "E214", {"points": [v(5.88, 18.07) * mm, v(5.93, 18.07) * mm, v(6.14, 18.2) * mm, v(6.35, 18.36) * mm]});
            skFitSpline(sketch, "E215", {"points": [v(6.35, 18.36) * mm, v(6.55, 18.52) * mm, v(6.85, 18.71) * mm, v(7, 18.79) * mm]});
            skLineSegment(sketch, "E216", {"start": v(2.66, 17.42) * mm, "end": v(2.87, 17.65) * mm});
            skLineSegment(sketch, "E217", {"start": v(2.87, 17.65) * mm, "end": v(2.93, 17.42) * mm});
            skLineSegment(sketch, "E218", {"start": v(2.93, 17.42) * mm, "end": v(2.66, 17.42) * mm});
            skFitSpline(sketch, "E219", {"points": [v(7.2, 18.8) * mm, v(7.05, 18.6) * mm, v(7.09, 18.24) * mm, v(7.25, 18.24) * mm]});
            skFitSpline(sketch, "E220", {"points": [v(7.25, 18.24) * mm, v(7.29, 18.24) * mm, v(7.48, 18.33) * mm, v(7.68, 18.44) * mm]});
            skFitSpline(sketch, "E221", {"points": [v(7.68, 18.44) * mm, v(8.03, 18.63) * mm, v(8.33, 18.76) * mm, v(8.64, 18.83) * mm]});
            skLineSegment(sketch, "E222", {"start": v(7, 18.79) * mm, "end": v(7.28, 18.93) * mm});
            skLineSegment(sketch, "E223", {"start": v(7.28, 18.93) * mm, "end": v(7.2, 18.8) * mm});
            skLineSegment(sketch, "E224", {"start": v(7.2, 18.8) * mm, "end": v(7, 18.79) * mm});
            skFitSpline(sketch, "E225", {"points": [v(8.66, 18.66) * mm, v(8.5, 18.43) * mm, v(8.48, 18.26) * mm, v(8.6, 18.21) * mm]});
            skFitSpline(sketch, "E226", {"points": [v(8.6, 18.21) * mm, v(8.64, 18.2) * mm, v(8.92, 18.25) * mm, v(9.2, 18.35) * mm]});
            skFitSpline(sketch, "E227", {"points": [v(9.2, 18.35) * mm, v(9.5, 18.44) * mm, v(9.85, 18.53) * mm, v(9.98, 18.56) * mm]});
            skLineSegment(sketch, "E228", {"start": v(8.64, 18.83) * mm, "end": v(8.8, 18.87) * mm});
            skLineSegment(sketch, "E229", {"start": v(8.8, 18.87) * mm, "end": v(8.66, 18.66) * mm});
            skLineSegment(sketch, "E230", {"start": v(8.66, 18.66) * mm, "end": v(8.64, 18.83) * mm});
            skFitSpline(sketch, "E231", {"points": [v(10.08, 18.45) * mm, v(9.99, 18.36) * mm, v(9.93, 18.24) * mm, v(9.93, 18.13) * mm]});
            skFitSpline(sketch, "E232", {"points": [v(9.93, 18.13) * mm, v(9.93, 17.98) * mm, v(9.95, 17.96) * mm, v(10.1, 17.96) * mm]});
            skFitSpline(sketch, "E233", {"points": [v(10.1, 17.96) * mm, v(10.18, 17.96) * mm, v(10.46, 18.01) * mm, v(10.7, 18.07) * mm]});
            skFitSpline(sketch, "E234", {"points": [v(10.7, 18.07) * mm, v(10.96, 18.14) * mm, v(11.33, 18.19) * mm, v(11.6, 18.19) * mm]});
            skLineSegment(sketch, "E235", {"start": v(9.98, 18.56) * mm, "end": v(10.22, 18.6) * mm});
            skLineSegment(sketch, "E236", {"start": v(10.22, 18.6) * mm, "end": v(10.08, 18.45) * mm});
            skLineSegment(sketch, "E237", {"start": v(10.08, 18.45) * mm, "end": v(9.98, 18.56) * mm});
            skFitSpline(sketch, "E238", {"points": [v(11.84, 17.97) * mm, v(11.73, 17.85) * mm, v(11.63, 17.73) * mm, v(11.63, 17.7) * mm]});
            skFitSpline(sketch, "E239", {"points": [v(11.63, 17.7) * mm, v(11.63, 17.62) * mm, v(12.1, 17.57) * mm, v(12.81, 17.56) * mm]});
            skFitSpline(sketch, "E240", {"points": [v(12.81, 17.56) * mm, v(13.13, 17.56) * mm, v(13.4, 17.55) * mm, v(13.4, 17.54) * mm]});
            skFitSpline(sketch, "E241", {"points": [v(13.4, 17.54) * mm, v(13.4, 17.52) * mm, v(13.33, 17.42) * mm, v(13.25, 17.31) * mm]});
            skFitSpline(sketch, "E242", {"points": [v(13.25, 17.31) * mm, v(13.1, 17.08) * mm, v(12.77, 16.31) * mm, v(12.77, 16.17) * mm]});
            skFitSpline(sketch, "E243", {"points": [v(12.77, 16.17) * mm, v(12.77, 16.09) * mm, v(12.81, 16.08) * mm, v(13.17, 16.12) * mm]});
            skFitSpline(sketch, "E244", {"points": [v(13.17, 16.12) * mm, v(13.5, 16.15) * mm, v(13.56, 16.14) * mm, v(13.53, 16.08) * mm]});
            skFitSpline(sketch, "E245", {"points": [v(13.53, 16.08) * mm, v(13.4, 15.86) * mm, v(13.11, 15.56) * mm, v(12.82, 15.32) * mm]});
            skFitSpline(sketch, "E246", {"points": [v(12.82, 15.32) * mm, v(12.29, 14.9) * mm, v(12.3, 14.72) * mm, v(12.9, 14.74) * mm]});
            skFitSpline(sketch, "E247", {"points": [v(12.9, 14.74) * mm, v(13.07, 14.75) * mm, v(13.22, 14.74) * mm, v(13.22, 14.73) * mm]});
            skFitSpline(sketch, "E248", {"points": [v(13.22, 14.73) * mm, v(13.22, 14.7) * mm, v(12.95, 14.43) * mm, v(12.63, 14.11) * mm]});
            skFitSpline(sketch, "E249", {"points": [v(12.63, 14.11) * mm, v(12.3, 13.8) * mm, v(12.03, 13.51) * mm, v(12.03, 13.49) * mm]});
            skFitSpline(sketch, "E250", {"points": [v(12.03, 13.49) * mm, v(12.03, 13.41) * mm, v(12.19, 13.37) * mm, v(12.47, 13.37) * mm]});
            skLineSegment(sketch, "E251", {"start": v(11.6, 18.19) * mm, "end": v(12.05, 18.19) * mm});
            skLineSegment(sketch, "E252", {"start": v(12.05, 18.19) * mm, "end": v(11.84, 17.97) * mm});
            skLineSegment(sketch, "E253", {"start": v(11.84, 17.97) * mm, "end": v(11.6, 18.19) * mm});
            skFitSpline(sketch, "E254", {"points": [v(12.46, 13.1) * mm, v(12.3, 12.96) * mm, v(11.99, 12.72) * mm, v(11.76, 12.57) * mm]});
            skFitSpline(sketch, "E255", {"points": [v(11.76, 12.57) * mm, v(11.54, 12.42) * mm, v(11.35, 12.26) * mm, v(11.35, 12.22) * mm]});
            skFitSpline(sketch, "E256", {"points": [v(11.35, 12.22) * mm, v(11.35, 12.12) * mm, v(11.53, 12.07) * mm, v(11.83, 12.07) * mm]});
            skLineSegment(sketch, "E257", {"start": v(12.47, 13.37) * mm, "end": v(12.74, 13.37) * mm});
            skLineSegment(sketch, "E258", {"start": v(12.74, 13.37) * mm, "end": v(12.46, 13.1) * mm});
            skLineSegment(sketch, "E259", {"start": v(12.46, 13.1) * mm, "end": v(12.47, 13.37) * mm});
            skFitSpline(sketch, "E260", {"points": [v(11.75, 11.84) * mm, v(11.58, 11.72) * mm, v(11.19, 11.5) * mm, v(10.89, 11.35) * mm]});
            skFitSpline(sketch, "E261", {"points": [v(10.89, 11.35) * mm, v(10.55, 11.18) * mm, v(10.34, 11.04) * mm, v(10.33, 10.99) * mm]});
            skFitSpline(sketch, "E262", {"points": [v(10.33, 10.99) * mm, v(10.33, 10.88) * mm, v(10.56, 10.77) * mm, v(10.8, 10.76) * mm]});
            skFitSpline(sketch, "E263", {"points": [v(10.8, 10.76) * mm, v(10.97, 10.76) * mm, v(10.97, 10.75) * mm, v(10.65, 10.6) * mm]});
            skFitSpline(sketch, "E264", {"points": [v(10.65, 10.6) * mm, v(10.47, 10.5) * mm, v(10.07, 10.36) * mm, v(9.76, 10.28) * mm]});
            skFitSpline(sketch, "E265", {"points": [v(9.76, 10.28) * mm, v(9.27, 10.14) * mm, v(9.2, 10.1) * mm, v(9.2, 10) * mm]});
            skFitSpline(sketch, "E266", {"points": [v(9.2, 10) * mm, v(9.2, 9.9) * mm, v(9.26, 9.84) * mm, v(9.4, 9.77) * mm]});
            skFitSpline(sketch, "E267", {"points": [v(9.4, 9.77) * mm, v(9.61, 9.67) * mm, v(9.62, 9.67) * mm, v(9.49, 9.62) * mm]});
            skFitSpline(sketch, "E268", {"points": [v(9.49, 9.62) * mm, v(9.27, 9.54) * mm, v(8.4, 9.4) * mm, v(8.12, 9.4) * mm]});
            skFitSpline(sketch, "E269", {"points": [v(8.12, 9.4) * mm, v(7.76, 9.4) * mm, v(7.67, 9.36) * mm, v(7.67, 9.2) * mm]});
            skFitSpline(sketch, "E270", {"points": [v(7.67, 9.2) * mm, v(7.67, 9.1) * mm, v(7.73, 9.03) * mm, v(7.84, 8.96) * mm]});
            skFitSpline(sketch, "E271", {"points": [v(7.84, 8.96) * mm, v(7.93, 8.9) * mm, v(8, 8.84) * mm, v(7.97, 8.82) * mm]});
            skFitSpline(sketch, "E272", {"points": [v(7.97, 8.82) * mm, v(7.9, 8.76) * mm, v(7.23, 8.79) * mm, v(6.68, 8.87) * mm]});
            skLineSegment(sketch, "E273", {"start": v(11.83, 12.07) * mm, "end": v(12.06, 12.07) * mm});
            skLineSegment(sketch, "E274", {"start": v(12.06, 12.07) * mm, "end": v(11.75, 11.84) * mm});
            skLineSegment(sketch, "E275", {"start": v(11.75, 11.84) * mm, "end": v(11.83, 12.07) * mm});
            skSolve(sketch);
        }
        {
            var Q0;
            Q0=makeQuery(id+"FgwKYBdbGhJWKQG_1.imprint","IMPRINT",FACE,{"disambiguationData":[TD([[makeQuery(id+"FgwKYBdbGhJWKQG_1.imprint","IMPRINT",EDGE,{"derivedFrom":sQuery(id+"FgwKYBdbGhJWKQG_1.wireOp",EDGE,"7f60fdca-cdcd-49b8-8de1-fb1aa7bb9cac")}),1.0]])]});
            var Q1;
            Q1=makeQuery(id+"FgwKYBdbGhJWKQG_1.imprint","IMPRINT",FACE,{"disambiguationData":[TD([[makeQuery(id+"FgwKYBdbGhJWKQG_1.imprint","IMPRINT",EDGE,{"derivedFrom":sQuery(id+"FgwKYBdbGhJWKQG_1.wireOp",EDGE,"0d085cb4-8bda-4499-815e-8f091fbd4b33")}),1.0]])]});
            var Q2;
            Q2=makeQuery(id+"FgwKYBdbGhJWKQG_1.imprint","IMPRINT",FACE,{"disambiguationData":[TD([[makeQuery(id+"FgwKYBdbGhJWKQG_1.imprint","IMPRINT",EDGE,{"derivedFrom":sQuery(id+"FgwKYBdbGhJWKQG_1.wireOp",EDGE,"f616bad8-dd80-48d3-aa4d-5a03fdac8b7b")}),1.0]])]});
            var Q3;
            Q3=makeQuery(id+"FgwKYBdbGhJWKQG_1.imprint","IMPRINT",FACE,{"disambiguationData":[TD([[makeQuery(id+"FgwKYBdbGhJWKQG_1.imprint","IMPRINT",EDGE,{"derivedFrom":sQuery(id+"FgwKYBdbGhJWKQG_1.wireOp",EDGE,"0836642a-d368-4bcc-99b0-16a3ca3f7264")}),1.0]])]});
            var Q4;
            Q4=makeQuery(id+"FgwKYBdbGhJWKQG_1.imprint","IMPRINT",FACE,{"disambiguationData":[TD([[makeQuery(id+"FgwKYBdbGhJWKQG_1.imprint","IMPRINT",EDGE,{"derivedFrom":sQuery(id+"FgwKYBdbGhJWKQG_1.wireOp",EDGE,"d69e1352-9020-4a84-acbb-b09646638222")}),1.0]])]});
            var Q5;
            Q5=makeQuery(id+"FgwKYBdbGhJWKQG_1.imprint","IMPRINT",FACE,{"disambiguationData":[TD([[makeQuery(id+"FgwKYBdbGhJWKQG_1.imprint","IMPRINT",EDGE,{"derivedFrom":sQuery(id+"FgwKYBdbGhJWKQG_1.wireOp",EDGE,"c626745b-f950-4033-a4fe-d9633b1f31a1")}),1.0]])]});
            var Q6;
            Q6=makeQuery(id+"FgwKYBdbGhJWKQG_1.imprint","IMPRINT",FACE,{"disambiguationData":[TD([[makeQuery(id+"FgwKYBdbGhJWKQG_1.imprint","IMPRINT",EDGE,{"derivedFrom":sQuery(id+"FgwKYBdbGhJWKQG_1.wireOp",EDGE,"e7ba4805-f87d-4e42-acb8-97aa786f36ac")}),1.0]])]});
            var Q7;
            Q7 = qSketchRegion(id + "F8", true);
            extrude(context, id + "F9", {"entities" : qUnion([Q0, Q1, Q2, Q3, Q4, Q5, Q6, Q7]), "operationType" : NewBodyOperationType.REMOVE, "oppositeDirection" : true, "depth" : 28 * mm, "offsetDistance" : 25 * mm});
        }
    });
